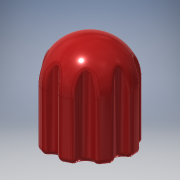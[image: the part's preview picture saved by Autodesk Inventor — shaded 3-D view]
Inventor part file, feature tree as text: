
AUTODESK INVENTOR PART (.ipt)
format: ipt  version: 2018 (Build 220112000, 112)  size: 413,696 bytes
history: native  units: mm
features: sketch x2, revolve x1, extrude x1, fillet x1
ambient origin geometry x8: Origin, YZ Plane, XZ Plane, XY Plane, X Axis, Y Axis, Z Axis, Center Point
bodies: Solid1 (feature_tree)
feature tree (5):
  revolve  "Revolution1"  [1 undecoded]
  extrude  "Extrusion1"  Depth=2.0mm
  fillet  "Fillet1"  Radius=2.0mm
  sketch  "Sketch1"  dims[d0=5.0mm d1=17.0mm]
  sketch  "Sketch2"  dims[d2=21.13mm d3=23.0mm d4=2.0mm d5=1.0mm d6=90.0deg d7=17.0mm d8=6.0mm d9=80.0mm d11=360.0deg d13=10.0mm d14=0.0mm d15=2.0mm]
note: 1 required parameter value undecoded (feature->parameter linkage not recoverable at this tier; creation-order binding heuristic only, values carry confidence <= 0.55)
